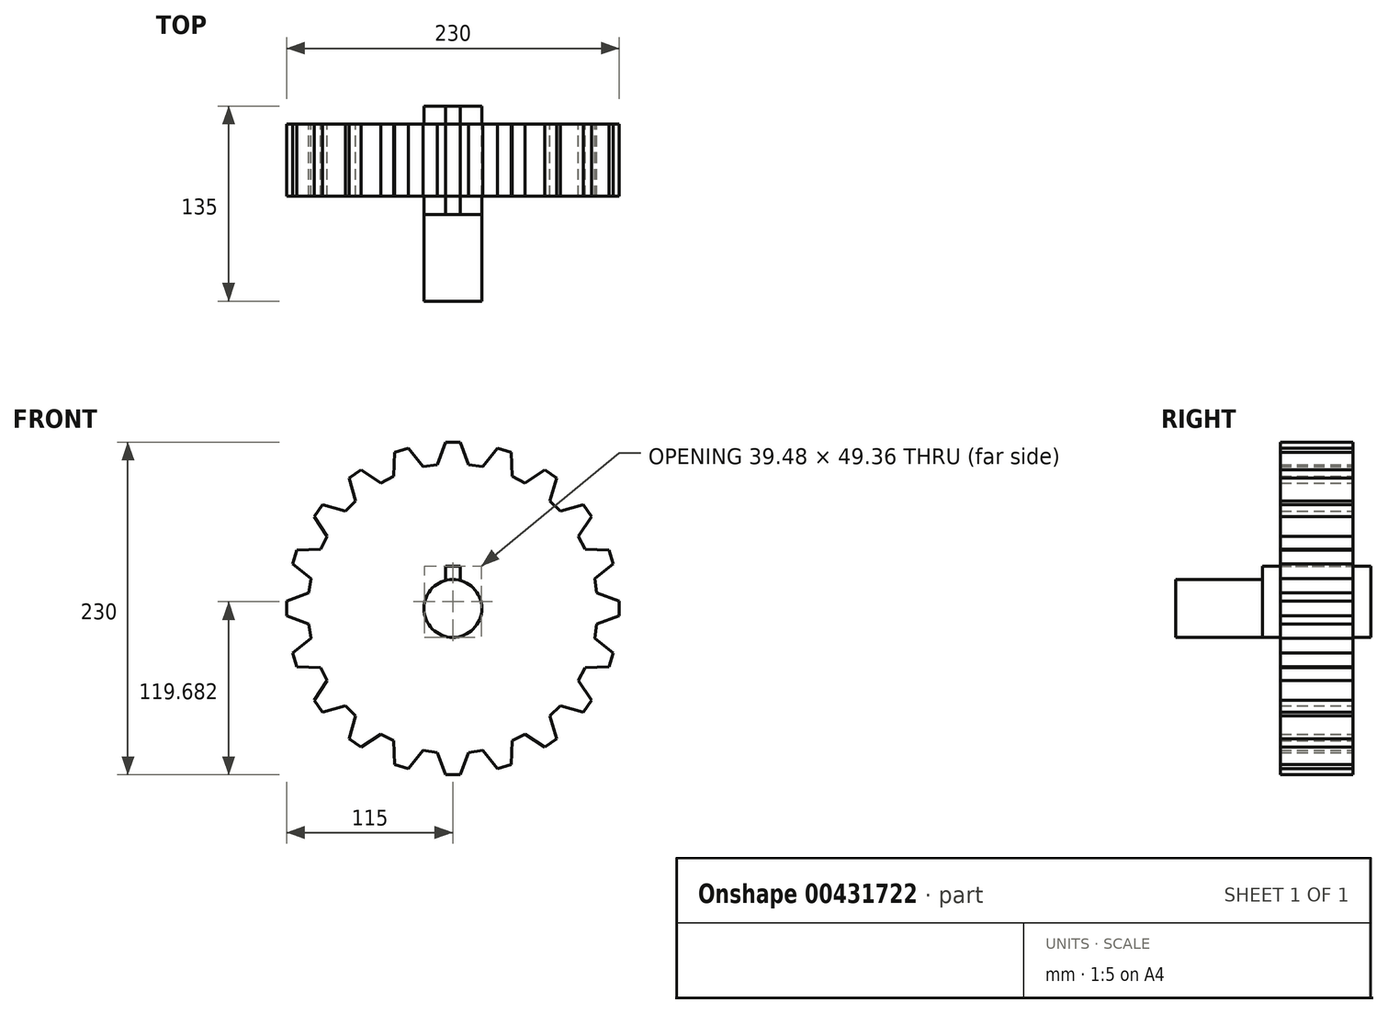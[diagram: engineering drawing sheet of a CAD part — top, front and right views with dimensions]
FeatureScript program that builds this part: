
annotation { "Feature Type Name" : "Feature", "Feature Type Description" : "" }
export const myFeature = defineFeature(function(context is Context, id is Id, definition is map)
    precondition{}
    {
        {
            var Q0;
            Q0=qCreatedBy(makeId("Front.planeOp"),FACE);
            var sketch = newSketch(context, id + "F0", { "sketchPlane" : qUnion([Q0])});
            skCircle(sketch, "E0", {"center": v(0, 0) * mm, "radius": 100 * mm, "construction": true});
            skLineSegment(sketch, "E1", {"start": v(0, -133.4) * mm, "end": v(0, 144.05) * mm, "construction": true});
            skLineSegment(sketch, "E2", {"start": v(-128.08, 0) * mm, "end": v(175.94, 0) * mm, "construction": true});
            skLineSegment(sketch, "E3", {"start": v(0, 0) * mm, "end": v(26.01, 164.24) * mm, "construction": true});
            skLineSegment(sketch, "E4", {"start": v(0, 0) * mm, "end": v(76.12, 149.4) * mm, "construction": true});
            skLineSegment(sketch, "E5", {"start": v(0, 115) * mm, "end": v(5, 115) * mm});
            skLineSegment(sketch, "E6", {"start": v(10.7, 99.55) * mm, "end": v(20.58, 97.99) * mm});
            skPoint(sketch, "E7", {"position": v(15.64, 98.77) * mm});
            skLineSegment(sketch, "E8", {"start": v(5, 115) * mm, "end": v(10.7, 99.55) * mm});
            skLineSegment(sketch, "E9.MirrorCS", {"start": v(30.78, 110.92) * mm, "end": v(20.58, 97.99) * mm});
            skLineSegment(sketch, "E10.MirrorCS", {"start": v(35.54, 109.37) * mm, "end": v(30.78, 110.92) * mm});
            skLineSegment(sketch, "E11.1.0", {"start": v(-30.78, 110.92) * mm, "end": v(-20.58, 97.99) * mm});
            skLineSegment(sketch, "E11.1.1", {"start": v(-35.54, 109.37) * mm, "end": v(-30.78, 110.92) * mm});
            skLineSegment(sketch, "E11.1.2", {"start": v(-20.58, 97.99) * mm, "end": v(-10.7, 99.55) * mm});
            skLineSegment(sketch, "E11.1.3", {"start": v(-5, 115) * mm, "end": v(-10.7, 99.55) * mm});
            skLineSegment(sketch, "E11.1.4", {"start": v(0, 115) * mm, "end": v(-5, 115) * mm});
            skLineSegment(sketch, "E11.2.0", {"start": v(-63.55, 95.98) * mm, "end": v(-49.85, 86.83) * mm});
            skLineSegment(sketch, "E11.2.1", {"start": v(-67.6, 93.04) * mm, "end": v(-63.55, 95.98) * mm});
            skLineSegment(sketch, "E11.2.2", {"start": v(-49.85, 86.83) * mm, "end": v(-40.94, 91.37) * mm});
            skLineSegment(sketch, "E11.2.3", {"start": v(-40.3, 107.83) * mm, "end": v(-40.94, 91.37) * mm});
            skLineSegment(sketch, "E11.2.4", {"start": v(-35.54, 109.37) * mm, "end": v(-40.3, 107.83) * mm});
            skLineSegment(sketch, "E11.3.0", {"start": v(-90.1, 71.64) * mm, "end": v(-74.25, 67.18) * mm});
            skLineSegment(sketch, "E11.3.1", {"start": v(-93.04, 67.6) * mm, "end": v(-90.1, 71.64) * mm});
            skLineSegment(sketch, "E11.3.2", {"start": v(-74.25, 67.18) * mm, "end": v(-67.18, 74.25) * mm});
            skLineSegment(sketch, "E11.3.3", {"start": v(-71.64, 90.1) * mm, "end": v(-67.18, 74.25) * mm});
            skLineSegment(sketch, "E11.3.4", {"start": v(-67.6, 93.04) * mm, "end": v(-71.64, 90.1) * mm});
            skLineSegment(sketch, "E11.4.0", {"start": v(-107.83, 40.3) * mm, "end": v(-91.37, 40.94) * mm});
            skLineSegment(sketch, "E11.4.1", {"start": v(-109.37, 35.54) * mm, "end": v(-107.83, 40.3) * mm});
            skLineSegment(sketch, "E11.4.2", {"start": v(-91.37, 40.94) * mm, "end": v(-86.83, 49.85) * mm});
            skLineSegment(sketch, "E11.4.3", {"start": v(-95.98, 63.55) * mm, "end": v(-86.83, 49.85) * mm});
            skLineSegment(sketch, "E11.4.4", {"start": v(-93.04, 67.6) * mm, "end": v(-95.98, 63.55) * mm});
            skLineSegment(sketch, "E11.5.0", {"start": v(-115, 5) * mm, "end": v(-99.55, 10.7) * mm});
            skLineSegment(sketch, "E11.5.1", {"start": v(-115, 0) * mm, "end": v(-115, 5) * mm});
            skLineSegment(sketch, "E11.5.2", {"start": v(-99.55, 10.7) * mm, "end": v(-97.99, 20.58) * mm});
            skLineSegment(sketch, "E11.5.3", {"start": v(-110.92, 30.78) * mm, "end": v(-97.99, 20.58) * mm});
            skLineSegment(sketch, "E11.5.4", {"start": v(-109.37, 35.54) * mm, "end": v(-110.92, 30.78) * mm});
            skLineSegment(sketch, "E11.6.0", {"start": v(-110.92, -30.78) * mm, "end": v(-97.99, -20.58) * mm});
            skLineSegment(sketch, "E11.6.1", {"start": v(-109.37, -35.54) * mm, "end": v(-110.92, -30.78) * mm});
            skLineSegment(sketch, "E11.6.2", {"start": v(-97.99, -20.58) * mm, "end": v(-99.55, -10.7) * mm});
            skLineSegment(sketch, "E11.6.3", {"start": v(-115, -5) * mm, "end": v(-99.55, -10.7) * mm});
            skLineSegment(sketch, "E11.6.4", {"start": v(-115, 0) * mm, "end": v(-115, -5) * mm});
            skLineSegment(sketch, "E11.7.0", {"start": v(-95.98, -63.55) * mm, "end": v(-86.83, -49.85) * mm});
            skLineSegment(sketch, "E11.7.1", {"start": v(-93.04, -67.6) * mm, "end": v(-95.98, -63.55) * mm});
            skLineSegment(sketch, "E11.7.2", {"start": v(-86.83, -49.85) * mm, "end": v(-91.37, -40.94) * mm});
            skLineSegment(sketch, "E11.7.3", {"start": v(-107.83, -40.3) * mm, "end": v(-91.37, -40.94) * mm});
            skLineSegment(sketch, "E11.7.4", {"start": v(-109.37, -35.54) * mm, "end": v(-107.83, -40.3) * mm});
            skLineSegment(sketch, "E11.8.0", {"start": v(-71.64, -90.1) * mm, "end": v(-67.18, -74.25) * mm});
            skLineSegment(sketch, "E11.8.1", {"start": v(-67.6, -93.04) * mm, "end": v(-71.64, -90.1) * mm});
            skLineSegment(sketch, "E11.8.2", {"start": v(-67.18, -74.25) * mm, "end": v(-74.25, -67.18) * mm});
            skLineSegment(sketch, "E11.8.3", {"start": v(-90.1, -71.64) * mm, "end": v(-74.25, -67.18) * mm});
            skLineSegment(sketch, "E11.8.4", {"start": v(-93.04, -67.6) * mm, "end": v(-90.1, -71.64) * mm});
            skLineSegment(sketch, "E11.9.0", {"start": v(-40.3, -107.83) * mm, "end": v(-40.94, -91.37) * mm});
            skLineSegment(sketch, "E11.9.1", {"start": v(-35.54, -109.37) * mm, "end": v(-40.3, -107.83) * mm});
            skLineSegment(sketch, "E11.9.2", {"start": v(-40.94, -91.37) * mm, "end": v(-49.85, -86.83) * mm});
            skLineSegment(sketch, "E11.9.3", {"start": v(-63.55, -95.98) * mm, "end": v(-49.85, -86.83) * mm});
            skLineSegment(sketch, "E11.9.4", {"start": v(-67.6, -93.04) * mm, "end": v(-63.55, -95.98) * mm});
            skLineSegment(sketch, "E11.10.0", {"start": v(-5, -115) * mm, "end": v(-10.7, -99.55) * mm});
            skLineSegment(sketch, "E11.10.1", {"start": v(0, -115) * mm, "end": v(-5, -115) * mm});
            skLineSegment(sketch, "E11.10.2", {"start": v(-10.7, -99.55) * mm, "end": v(-20.58, -97.99) * mm});
            skLineSegment(sketch, "E11.10.3", {"start": v(-30.78, -110.92) * mm, "end": v(-20.58, -97.99) * mm});
            skLineSegment(sketch, "E11.10.4", {"start": v(-35.54, -109.37) * mm, "end": v(-30.78, -110.92) * mm});
            skLineSegment(sketch, "E11.11.0", {"start": v(30.78, -110.92) * mm, "end": v(20.58, -97.99) * mm});
            skLineSegment(sketch, "E11.11.1", {"start": v(35.54, -109.37) * mm, "end": v(30.78, -110.92) * mm});
            skLineSegment(sketch, "E11.11.2", {"start": v(20.58, -97.99) * mm, "end": v(10.7, -99.55) * mm});
            skLineSegment(sketch, "E11.11.3", {"start": v(5, -115) * mm, "end": v(10.7, -99.55) * mm});
            skLineSegment(sketch, "E11.11.4", {"start": v(0, -115) * mm, "end": v(5, -115) * mm});
            skLineSegment(sketch, "E11.12.0", {"start": v(63.55, -95.98) * mm, "end": v(49.85, -86.83) * mm});
            skLineSegment(sketch, "E11.12.1", {"start": v(67.6, -93.04) * mm, "end": v(63.55, -95.98) * mm});
            skLineSegment(sketch, "E11.12.2", {"start": v(49.85, -86.83) * mm, "end": v(40.94, -91.37) * mm});
            skLineSegment(sketch, "E11.12.3", {"start": v(40.3, -107.83) * mm, "end": v(40.94, -91.37) * mm});
            skLineSegment(sketch, "E11.12.4", {"start": v(35.54, -109.37) * mm, "end": v(40.3, -107.83) * mm});
            skLineSegment(sketch, "E11.13.0", {"start": v(90.1, -71.64) * mm, "end": v(74.25, -67.18) * mm});
            skLineSegment(sketch, "E11.13.1", {"start": v(93.04, -67.6) * mm, "end": v(90.1, -71.64) * mm});
            skLineSegment(sketch, "E11.13.2", {"start": v(74.25, -67.18) * mm, "end": v(67.18, -74.25) * mm});
            skLineSegment(sketch, "E11.13.3", {"start": v(71.64, -90.1) * mm, "end": v(67.18, -74.25) * mm});
            skLineSegment(sketch, "E11.13.4", {"start": v(67.6, -93.04) * mm, "end": v(71.64, -90.1) * mm});
            skLineSegment(sketch, "E11.14.0", {"start": v(107.83, -40.3) * mm, "end": v(91.37, -40.94) * mm});
            skLineSegment(sketch, "E11.14.1", {"start": v(109.37, -35.54) * mm, "end": v(107.83, -40.3) * mm});
            skLineSegment(sketch, "E11.14.2", {"start": v(91.37, -40.94) * mm, "end": v(86.83, -49.85) * mm});
            skLineSegment(sketch, "E11.14.3", {"start": v(95.98, -63.55) * mm, "end": v(86.83, -49.85) * mm});
            skLineSegment(sketch, "E11.14.4", {"start": v(93.04, -67.6) * mm, "end": v(95.98, -63.55) * mm});
            skLineSegment(sketch, "E11.15.0", {"start": v(115, -5) * mm, "end": v(99.55, -10.7) * mm});
            skLineSegment(sketch, "E11.15.1", {"start": v(115, 0) * mm, "end": v(115, -5) * mm});
            skLineSegment(sketch, "E11.15.2", {"start": v(99.55, -10.7) * mm, "end": v(97.99, -20.58) * mm});
            skLineSegment(sketch, "E11.15.3", {"start": v(110.92, -30.78) * mm, "end": v(97.99, -20.58) * mm});
            skLineSegment(sketch, "E11.15.4", {"start": v(109.37, -35.54) * mm, "end": v(110.92, -30.78) * mm});
            skLineSegment(sketch, "E11.16.0", {"start": v(110.92, 30.78) * mm, "end": v(97.99, 20.58) * mm});
            skLineSegment(sketch, "E11.16.1", {"start": v(109.37, 35.54) * mm, "end": v(110.92, 30.78) * mm});
            skLineSegment(sketch, "E11.16.2", {"start": v(97.99, 20.58) * mm, "end": v(99.55, 10.7) * mm});
            skLineSegment(sketch, "E11.16.3", {"start": v(115, 5) * mm, "end": v(99.55, 10.7) * mm});
            skLineSegment(sketch, "E11.16.4", {"start": v(115, 0) * mm, "end": v(115, 5) * mm});
            skLineSegment(sketch, "E11.17.0", {"start": v(95.98, 63.55) * mm, "end": v(86.83, 49.85) * mm});
            skLineSegment(sketch, "E11.17.1", {"start": v(93.04, 67.6) * mm, "end": v(95.98, 63.55) * mm});
            skLineSegment(sketch, "E11.17.2", {"start": v(86.83, 49.85) * mm, "end": v(91.37, 40.94) * mm});
            skLineSegment(sketch, "E11.17.3", {"start": v(107.83, 40.3) * mm, "end": v(91.37, 40.94) * mm});
            skLineSegment(sketch, "E11.17.4", {"start": v(109.37, 35.54) * mm, "end": v(107.83, 40.3) * mm});
            skLineSegment(sketch, "E11.18.0", {"start": v(71.64, 90.1) * mm, "end": v(67.18, 74.25) * mm});
            skLineSegment(sketch, "E11.18.1", {"start": v(67.6, 93.04) * mm, "end": v(71.64, 90.1) * mm});
            skLineSegment(sketch, "E11.18.2", {"start": v(67.18, 74.25) * mm, "end": v(74.25, 67.18) * mm});
            skLineSegment(sketch, "E11.18.3", {"start": v(90.1, 71.64) * mm, "end": v(74.25, 67.18) * mm});
            skLineSegment(sketch, "E11.18.4", {"start": v(93.04, 67.6) * mm, "end": v(90.1, 71.64) * mm});
            skLineSegment(sketch, "E11.19.0", {"start": v(40.3, 107.83) * mm, "end": v(40.94, 91.37) * mm});
            skLineSegment(sketch, "E11.19.1", {"start": v(35.54, 109.37) * mm, "end": v(40.3, 107.83) * mm});
            skLineSegment(sketch, "E11.19.2", {"start": v(40.94, 91.37) * mm, "end": v(49.85, 86.83) * mm});
            skLineSegment(sketch, "E11.19.3", {"start": v(63.55, 95.98) * mm, "end": v(49.85, 86.83) * mm});
            skLineSegment(sketch, "E11.19.4", {"start": v(67.6, 93.04) * mm, "end": v(63.55, 95.98) * mm});
            skSolve(sketch);
        }
        {
            var Q0;
            Q0 = qSketchRegion(id + "F0", true);
            var Q1;
            Q1 = qConstructionFilter(qBodyType(qCreatedBy(id + "F0" ,EDGE), BodyType.WIRE), ConstructionObject.NO);
            extrude(context, id + "F1", {"entities" : qUnion([Q0]), "surfaceEntities" : qUnion([Q1]), "endBound" : BoundingType.SYMMETRIC, "depth" : 50 * mm});
        }
        {
            var Q0;
            Q0=qCreatedBy(makeId("Front.planeOp"),FACE);
            var sketch = newSketch(context, id + "F2", { "sketchPlane" : qUnion([Q0])});
            skArc(sketch, "E12", {"start": v(-6.36, 18.96) * mm, "mid": v(0, -20) * mm, "end": v(6.36, 18.96) * mm});
            skLineSegment(sketch, "E13", {"start": v(-5, 20.86) * mm, "end": v(-5, 29.36) * mm});
            skLineSegment(sketch, "E14", {"start": v(-5, 29.36) * mm, "end": v(5, 29.36) * mm});
            skLineSegment(sketch, "E15", {"start": v(5, 29.36) * mm, "end": v(5, 20.86) * mm});
            skPoint(sketch, "E16", {"position": v(0, 29.36) * mm});
            skPoint(sketch, "E17.visualSharp", {"position": v(5, 19.36) * mm});
            skArc(sketch, "E17.filletArc", {"start": v(5, 20.86) * mm, "mid": v(5.38, 19.69) * mm, "end": v(6.36, 18.96) * mm});
            skPoint(sketch, "E18.visualSharp", {"position": v(-5, 19.36) * mm});
            skArc(sketch, "E18.filletArc", {"start": v(-6.36, 18.96) * mm, "mid": v(-5.38, 19.69) * mm, "end": v(-5, 20.86) * mm});
            skSolve(sketch);
        }
        {
            var Q0;
            Q0 = qSketchRegion(id + "F2", true);
            extrude(context, id + "F3", {"entities" : qUnion([Q0]), "operationType" : NewBodyOperationType.REMOVE, "endBound" : BoundingType.SYMMETRIC, "oppositeDirection" : true, "depth" : 50 * mm});
        }
        {
            var Q0;
            Q0 = qSketchRegion(id + "F2", true);
            extrude(context, id + "F4", {"entities" : qUnion([Q0]), "endBound" : BoundingType.SYMMETRIC, "depth" : 75 * mm});
        }
        {
            var Q0;
            Q0=makeQuery(id+"F4.opExtrude","CAP_FACE",FACE,{"disambiguationData":[OSD([sQuery(id+"F2.wireOp",EDGE,"E12"),sQuery(id+"F2.wireOp",EDGE,"E13"),sQuery(id+"F2.wireOp",EDGE,"E14"),sQuery(id+"F2.wireOp",EDGE,"E15"),sQuery(id+"F2.wireOp",EDGE,"E17.filletArc"),sQuery(id+"F2.wireOp",EDGE,"E18.filletArc")])],"isStart":false});
            var sketch = newSketch(context, id + "F5", { "sketchPlane" : qUnion([Q0])});
            skCircle(sketch, "E19", {"center": v(0, 0) * mm, "radius": 20 * mm});
            skSolve(sketch);
        }
        {
            var Q0;
            Q0 = qSketchRegion(id + "F5", true);
            extrude(context, id + "F6", {"entities" : qUnion([Q0]), "depth" : 60 * mm});
        }
    });
